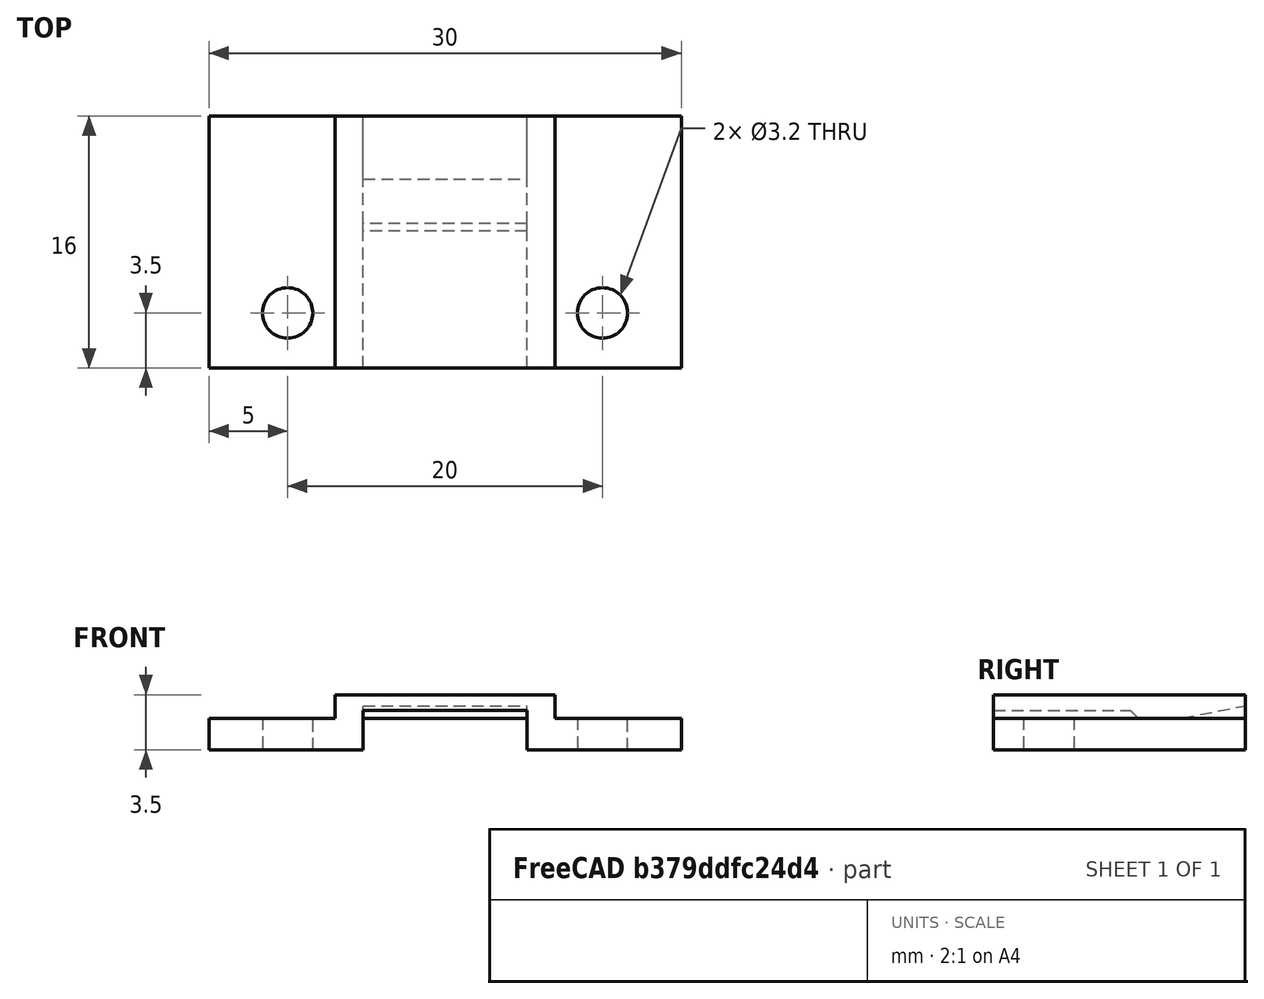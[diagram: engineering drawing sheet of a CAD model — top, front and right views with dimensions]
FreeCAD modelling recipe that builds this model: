
FCSTD DOCUMENT  (FreeCAD 0.21R33771 (Git))
Label: NodeHolder
License: Creative Commons Attribution-ShareAlike 4.0
LicenseURL: https://creativecommons.org/licenses/by-sa/4.0/
objects: Part::Box×5, Part::Cut×5, Part::Cylinder×2, Part::MultiFuse×2, Part::Chamfer×1, Part::Wedge×1
note: 16 computed .brp shape members not serialized (recipe doc carries the construction recipe); baked Part::Feature solids carry a one-line shape summary decoded from their .brp

FEATURE [Part::Box] Box  label="Würfel"
  AttacherType = Attacher::AttachEngine3D
  Height = 3.5
  Length = 30
  Placement = pos=(0,-7,0) rot=(0,0,1;0rad)
  Width = 16
FEATURE [Part::Box] Box001  label="Würfel001"
  AttacherType = Attacher::AttachEngine3D
  Height = 2
  Length = 10.4
  Placement = pos=(9.8,-7,0) rot=(0,0,1;0rad)
  Width = 16
FEATURE [Part::Cut] Cut
  Base = -> Box
  Tool = -> Box001
FEATURE [Part::Box] Box002  label="Würfel002"
  AttacherType = Attacher::AttachEngine3D
  Height = 1
  Length = 10.4
  Placement = pos=(9.8,-7,1.5) rot=(0,0,1;0rad)
  Width = 8.7
FEATURE [Part::Cut] Cut001
  Base = -> Cut
  Tool = -> Box002
FEATURE [Part::Cylinder] Cylinder  label="Zylinder"
  Angle = 360
  AttacherType = Attacher::AttachEngine3D
  FirstAngle = 0
  Height = 3.5
  Placement = pos=(5,4.5,0) rot=(0,0,1;0rad)
  Radius = 1.6
  SecondAngle = 0
FEATURE [Part::Cylinder] Cylinder001  label="Zylinder001"
  Angle = 360
  AttacherType = Attacher::AttachEngine3D
  FirstAngle = 0
  Height = 3.5
  Placement = pos=(25,4.5,0) rot=(0,0,1;0rad)
  Radius = 1.6
  SecondAngle = 0
FEATURE [Part::MultiFuse] Fusion
  Placement = pos=(0,-8,0) rot=(0,0,1;0rad)
  Shapes = -> [Cylinder,Cylinder001]
FEATURE [Part::Cut] Cut002  label="Cut3"
  Base = -> Cut001
  Tool = -> Fusion
FEATURE [Part::Box] Box003  label="Würfel003"
  AttacherType = Attacher::AttachEngine3D
  Height = 1.5
  Length = 8
  Placement = pos=(0,-7,2) rot=(0,0,1;0rad)
  Width = 16
FEATURE [Part::Box] Box004  label="Würfel004"
  AttacherType = Attacher::AttachEngine3D
  Height = 1.5
  Length = 8
  Placement = pos=(22,-7,2) rot=(0,0,1;0rad)
  Width = 16
FEATURE [Part::MultiFuse] Fusion001
  Shapes = -> [Box003,Box004]
FEATURE [Part::Cut] Cut003  label="Cut4"
  Base = -> Cut002
  Tool = -> Fusion001
FEATURE [Part::Chamfer] Chamfer
  Base = -> Cut003
  Edges = 1 edges r=0.49: [Edge57]
FEATURE [Part::Wedge] Wedge  label="Keil"
  AttacherType = Attacher::AttachEngine3D
  Placement = pos=(9.8,5,2) rot=(0,0,1;0rad)
  X2max = 10.4
  X2min = 0
  Xmax = 10.4
  Xmin = 0
  Ymax = 4
  Ymin = 0
  Z2max = 0.8
  Z2min = 0
  Zmax = 0.01
  Zmin = 0
FEATURE [Part::Cut] Cut004  label="Final"
  Base = -> Chamfer
  Tool = -> Wedge
